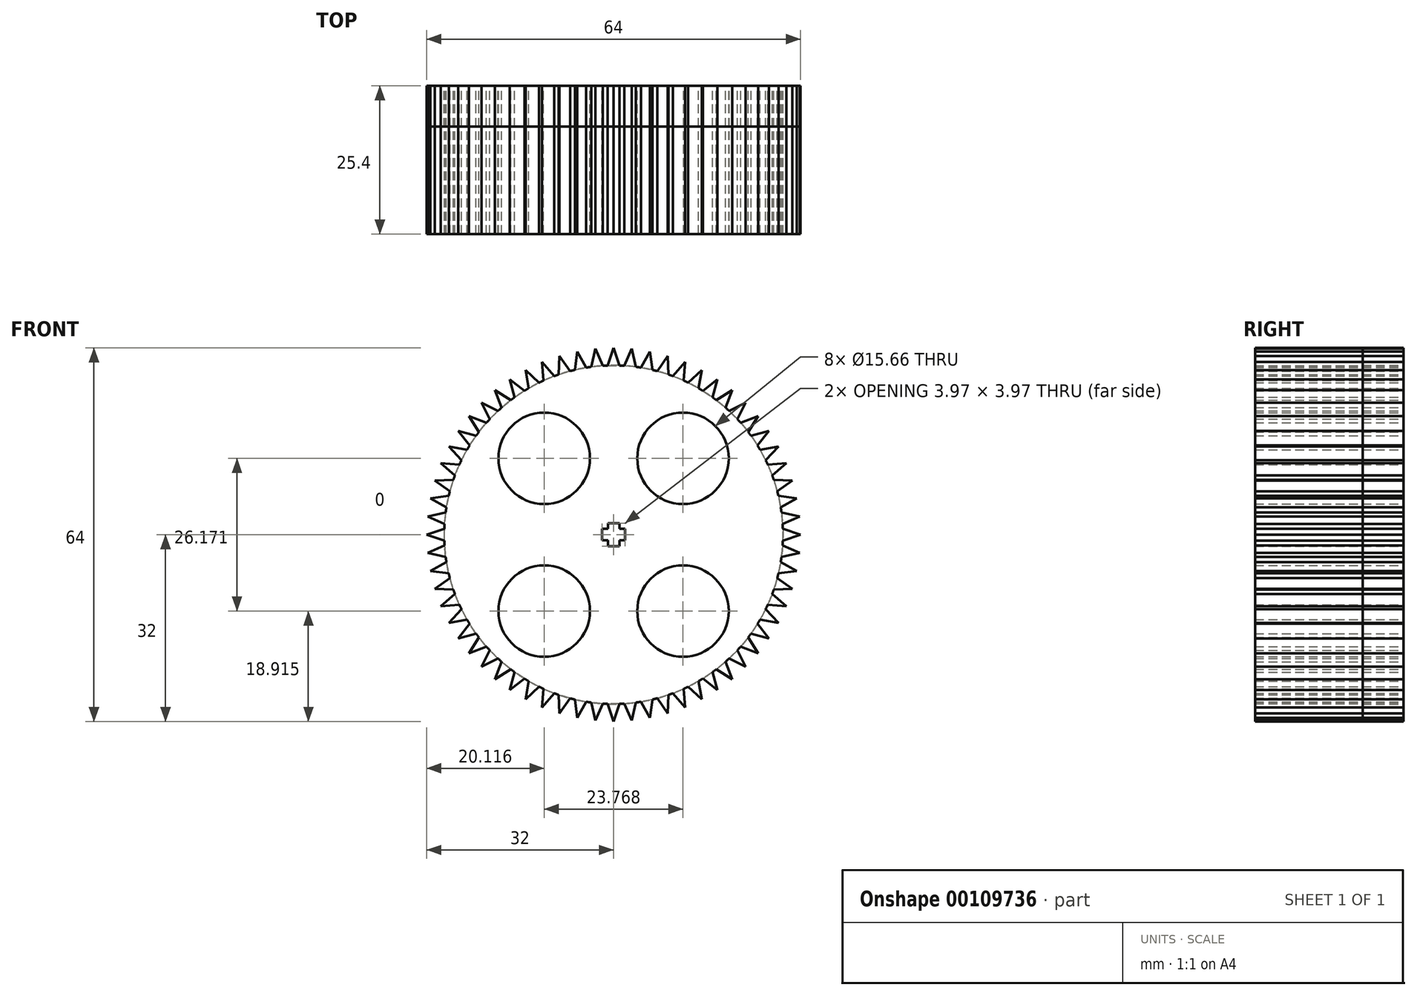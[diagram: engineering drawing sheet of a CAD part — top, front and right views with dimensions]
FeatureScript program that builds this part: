
annotation { "Feature Type Name" : "Feature", "Feature Type Description" : "" }
export const myFeature = defineFeature(function(context is Context, id is Id, definition is map)
    precondition{}
    {
        {
            var Q0;
            Q0=qCreatedBy(makeId("Front.planeOp"),FACE);
            var sketch = newSketch(context, id + "F0", { "sketchPlane" : qUnion([Q0])});
            skLineSegment(sketch, "E0", {"start": v(-0.98, 1.98) * mm, "end": v(-0.98, 0.98) * mm});
            skLineSegment(sketch, "E1", {"start": v(-0.98, 0.98) * mm, "end": v(-1.98, 0.98) * mm});
            skLineSegment(sketch, "E2.MirrorCS", {"start": v(0.98, 1.98) * mm, "end": v(0.98, 0.98) * mm});
            skLineSegment(sketch, "E3.MirrorCS", {"start": v(0.98, 0.98) * mm, "end": v(1.98, 0.98) * mm});
            skLineSegment(sketch, "E4.MirrorCS", {"start": v(0.98, -0.98) * mm, "end": v(1.98, -0.98) * mm});
            skLineSegment(sketch, "E5.MirrorCS", {"start": v(0.98, -1.98) * mm, "end": v(0.98, -0.98) * mm});
            skLineSegment(sketch, "E6.MirrorCS", {"start": v(-0.98, -1.98) * mm, "end": v(-0.98, -0.98) * mm});
            skLineSegment(sketch, "E7.MirrorCS", {"start": v(-0.98, -0.98) * mm, "end": v(-1.98, -0.98) * mm});
            skLineSegment(sketch, "E8", {"start": v(-0.98, 1.98) * mm, "end": v(0.98, 1.98) * mm});
            skLineSegment(sketch, "E9", {"start": v(-1.98, 0.98) * mm, "end": v(-1.98, -0.98) * mm});
            skLineSegment(sketch, "E10.MirrorCS", {"start": v(1.98, 0.98) * mm, "end": v(1.98, -0.98) * mm});
            skLineSegment(sketch, "E11.MirrorCS", {"start": v(-0.98, -1.98) * mm, "end": v(0.98, -1.98) * mm});
            skCircle(sketch, "E12", {"center": v(0, 0) * mm, "radius": 29 * mm});
            skLineSegment(sketch, "E13", {"start": v(-1, 28.98) * mm, "end": v(0, 32) * mm});
            skLineSegment(sketch, "E14.MirrorCS", {"start": v(1, 28.98) * mm, "end": v(0, 32) * mm});
            skLineSegment(sketch, "E15", {"start": v(-1, 28.98) * mm, "end": v(1, 28.98) * mm});
            skLineSegment(sketch, "E16.1.0", {"start": v(-1.85, 28.94) * mm, "end": v(-3.14, 31.85) * mm});
            skLineSegment(sketch, "E16.1.1", {"start": v(-3.84, 28.75) * mm, "end": v(-3.14, 31.85) * mm});
            skLineSegment(sketch, "E16.1.2", {"start": v(-3.84, 28.75) * mm, "end": v(-1.85, 28.94) * mm});
            skLineSegment(sketch, "E16.2.0", {"start": v(-4.67, 28.62) * mm, "end": v(-6.24, 31.39) * mm});
            skLineSegment(sketch, "E16.2.1", {"start": v(-6.64, 28.23) * mm, "end": v(-6.24, 31.39) * mm});
            skLineSegment(sketch, "E16.2.2", {"start": v(-6.64, 28.23) * mm, "end": v(-4.67, 28.62) * mm});
            skLineSegment(sketch, "E16.3.0", {"start": v(-7.46, 28.03) * mm, "end": v(-9.29, 30.62) * mm});
            skLineSegment(sketch, "E16.3.1", {"start": v(-9.37, 27.44) * mm, "end": v(-9.29, 30.62) * mm});
            skLineSegment(sketch, "E16.3.2", {"start": v(-9.37, 27.44) * mm, "end": v(-7.46, 28.03) * mm});
            skLineSegment(sketch, "E16.4.0", {"start": v(-10.17, 27.16) * mm, "end": v(-12.25, 29.56) * mm});
            skLineSegment(sketch, "E16.4.1", {"start": v(-12.02, 26.4) * mm, "end": v(-12.25, 29.56) * mm});
            skLineSegment(sketch, "E16.4.2", {"start": v(-12.02, 26.4) * mm, "end": v(-10.17, 27.16) * mm});
            skLineSegment(sketch, "E16.5.0", {"start": v(-12.78, 26.03) * mm, "end": v(-15.08, 28.22) * mm});
            skLineSegment(sketch, "E16.5.1", {"start": v(-14.54, 25.09) * mm, "end": v(-15.08, 28.22) * mm});
            skLineSegment(sketch, "E16.5.2", {"start": v(-14.54, 25.09) * mm, "end": v(-12.78, 26.03) * mm});
            skLineSegment(sketch, "E16.6.0", {"start": v(-15.27, 24.65) * mm, "end": v(-17.78, 26.6) * mm});
            skLineSegment(sketch, "E16.6.1", {"start": v(-16.93, 23.54) * mm, "end": v(-17.78, 26.6) * mm});
            skLineSegment(sketch, "E16.6.2", {"start": v(-16.93, 23.54) * mm, "end": v(-15.27, 24.65) * mm});
            skLineSegment(sketch, "E16.7.0", {"start": v(-17.61, 23.04) * mm, "end": v(-20.3, 24.74) * mm});
            skLineSegment(sketch, "E16.7.1", {"start": v(-19.16, 21.77) * mm, "end": v(-20.3, 24.74) * mm});
            skLineSegment(sketch, "E16.7.2", {"start": v(-19.16, 21.77) * mm, "end": v(-17.61, 23.04) * mm});
            skLineSegment(sketch, "E16.8.0", {"start": v(-19.79, 21.2) * mm, "end": v(-22.63, 22.63) * mm});
            skLineSegment(sketch, "E16.8.1", {"start": v(-21.2, 19.79) * mm, "end": v(-22.63, 22.63) * mm});
            skLineSegment(sketch, "E16.8.2", {"start": v(-21.2, 19.79) * mm, "end": v(-19.79, 21.2) * mm});
            skLineSegment(sketch, "E16.9.0", {"start": v(-21.77, 19.16) * mm, "end": v(-24.74, 20.3) * mm});
            skLineSegment(sketch, "E16.9.1", {"start": v(-23.04, 17.61) * mm, "end": v(-24.74, 20.3) * mm});
            skLineSegment(sketch, "E16.9.2", {"start": v(-23.04, 17.61) * mm, "end": v(-21.77, 19.16) * mm});
            skLineSegment(sketch, "E16.10.0", {"start": v(-23.54, 16.93) * mm, "end": v(-26.6, 17.78) * mm});
            skLineSegment(sketch, "E16.10.1", {"start": v(-24.65, 15.27) * mm, "end": v(-26.6, 17.78) * mm});
            skLineSegment(sketch, "E16.10.2", {"start": v(-24.65, 15.27) * mm, "end": v(-23.54, 16.93) * mm});
            skLineSegment(sketch, "E16.11.0", {"start": v(-25.09, 14.54) * mm, "end": v(-28.22, 15.08) * mm});
            skLineSegment(sketch, "E16.11.1", {"start": v(-26.03, 12.78) * mm, "end": v(-28.22, 15.08) * mm});
            skLineSegment(sketch, "E16.11.2", {"start": v(-26.03, 12.78) * mm, "end": v(-25.09, 14.54) * mm});
            skLineSegment(sketch, "E16.12.0", {"start": v(-26.4, 12.02) * mm, "end": v(-29.56, 12.25) * mm});
            skLineSegment(sketch, "E16.12.1", {"start": v(-27.16, 10.17) * mm, "end": v(-29.56, 12.25) * mm});
            skLineSegment(sketch, "E16.12.2", {"start": v(-27.16, 10.17) * mm, "end": v(-26.4, 12.02) * mm});
            skLineSegment(sketch, "E16.13.0", {"start": v(-27.44, 9.37) * mm, "end": v(-30.62, 9.29) * mm});
            skLineSegment(sketch, "E16.13.1", {"start": v(-28.03, 7.46) * mm, "end": v(-30.62, 9.29) * mm});
            skLineSegment(sketch, "E16.13.2", {"start": v(-28.03, 7.46) * mm, "end": v(-27.44, 9.37) * mm});
            skLineSegment(sketch, "E16.14.0", {"start": v(-28.23, 6.64) * mm, "end": v(-31.39, 6.24) * mm});
            skLineSegment(sketch, "E16.14.1", {"start": v(-28.62, 4.67) * mm, "end": v(-31.39, 6.24) * mm});
            skLineSegment(sketch, "E16.14.2", {"start": v(-28.62, 4.67) * mm, "end": v(-28.23, 6.64) * mm});
            skLineSegment(sketch, "E16.15.0", {"start": v(-28.75, 3.84) * mm, "end": v(-31.85, 3.14) * mm});
            skLineSegment(sketch, "E16.15.1", {"start": v(-28.94, 1.85) * mm, "end": v(-31.85, 3.14) * mm});
            skLineSegment(sketch, "E16.15.2", {"start": v(-28.94, 1.85) * mm, "end": v(-28.75, 3.84) * mm});
            skLineSegment(sketch, "E16.16.0", {"start": v(-28.98, 1) * mm, "end": v(-32, 0) * mm});
            skLineSegment(sketch, "E16.16.1", {"start": v(-28.98, -1) * mm, "end": v(-32, 0) * mm});
            skLineSegment(sketch, "E16.16.2", {"start": v(-28.98, -1) * mm, "end": v(-28.98, 1) * mm});
            skLineSegment(sketch, "E16.17.0", {"start": v(-28.94, -1.85) * mm, "end": v(-31.85, -3.14) * mm});
            skLineSegment(sketch, "E16.17.1", {"start": v(-28.75, -3.84) * mm, "end": v(-31.85, -3.14) * mm});
            skLineSegment(sketch, "E16.17.2", {"start": v(-28.75, -3.84) * mm, "end": v(-28.94, -1.85) * mm});
            skLineSegment(sketch, "E16.18.0", {"start": v(-28.62, -4.67) * mm, "end": v(-31.39, -6.24) * mm});
            skLineSegment(sketch, "E16.18.1", {"start": v(-28.23, -6.64) * mm, "end": v(-31.39, -6.24) * mm});
            skLineSegment(sketch, "E16.18.2", {"start": v(-28.23, -6.64) * mm, "end": v(-28.62, -4.67) * mm});
            skLineSegment(sketch, "E16.19.0", {"start": v(-28.03, -7.46) * mm, "end": v(-30.62, -9.29) * mm});
            skLineSegment(sketch, "E16.19.1", {"start": v(-27.44, -9.37) * mm, "end": v(-30.62, -9.29) * mm});
            skLineSegment(sketch, "E16.19.2", {"start": v(-27.44, -9.37) * mm, "end": v(-28.03, -7.46) * mm});
            skLineSegment(sketch, "E16.20.0", {"start": v(-27.16, -10.17) * mm, "end": v(-29.56, -12.25) * mm});
            skLineSegment(sketch, "E16.20.1", {"start": v(-26.4, -12.02) * mm, "end": v(-29.56, -12.25) * mm});
            skLineSegment(sketch, "E16.20.2", {"start": v(-26.4, -12.02) * mm, "end": v(-27.16, -10.17) * mm});
            skLineSegment(sketch, "E16.21.0", {"start": v(-26.03, -12.78) * mm, "end": v(-28.22, -15.08) * mm});
            skLineSegment(sketch, "E16.21.1", {"start": v(-25.09, -14.54) * mm, "end": v(-28.22, -15.08) * mm});
            skLineSegment(sketch, "E16.21.2", {"start": v(-25.09, -14.54) * mm, "end": v(-26.03, -12.78) * mm});
            skLineSegment(sketch, "E16.22.0", {"start": v(-24.65, -15.27) * mm, "end": v(-26.6, -17.78) * mm});
            skLineSegment(sketch, "E16.22.1", {"start": v(-23.54, -16.93) * mm, "end": v(-26.6, -17.78) * mm});
            skLineSegment(sketch, "E16.22.2", {"start": v(-23.54, -16.93) * mm, "end": v(-24.65, -15.27) * mm});
            skLineSegment(sketch, "E16.23.0", {"start": v(-23.04, -17.61) * mm, "end": v(-24.74, -20.3) * mm});
            skLineSegment(sketch, "E16.23.1", {"start": v(-21.77, -19.16) * mm, "end": v(-24.74, -20.3) * mm});
            skLineSegment(sketch, "E16.23.2", {"start": v(-21.77, -19.16) * mm, "end": v(-23.04, -17.61) * mm});
            skLineSegment(sketch, "E16.24.0", {"start": v(-21.2, -19.79) * mm, "end": v(-22.63, -22.63) * mm});
            skLineSegment(sketch, "E16.24.1", {"start": v(-19.79, -21.2) * mm, "end": v(-22.63, -22.63) * mm});
            skLineSegment(sketch, "E16.24.2", {"start": v(-19.79, -21.2) * mm, "end": v(-21.2, -19.79) * mm});
            skLineSegment(sketch, "E16.25.0", {"start": v(-19.16, -21.77) * mm, "end": v(-20.3, -24.74) * mm});
            skLineSegment(sketch, "E16.25.1", {"start": v(-17.61, -23.04) * mm, "end": v(-20.3, -24.74) * mm});
            skLineSegment(sketch, "E16.25.2", {"start": v(-17.61, -23.04) * mm, "end": v(-19.16, -21.77) * mm});
            skLineSegment(sketch, "E16.26.0", {"start": v(-16.93, -23.54) * mm, "end": v(-17.78, -26.6) * mm});
            skLineSegment(sketch, "E16.26.1", {"start": v(-15.27, -24.65) * mm, "end": v(-17.78, -26.6) * mm});
            skLineSegment(sketch, "E16.26.2", {"start": v(-15.27, -24.65) * mm, "end": v(-16.93, -23.54) * mm});
            skLineSegment(sketch, "E16.27.0", {"start": v(-14.54, -25.09) * mm, "end": v(-15.08, -28.22) * mm});
            skLineSegment(sketch, "E16.27.1", {"start": v(-12.78, -26.03) * mm, "end": v(-15.08, -28.22) * mm});
            skLineSegment(sketch, "E16.27.2", {"start": v(-12.78, -26.03) * mm, "end": v(-14.54, -25.09) * mm});
            skLineSegment(sketch, "E16.28.0", {"start": v(-12.02, -26.4) * mm, "end": v(-12.25, -29.56) * mm});
            skLineSegment(sketch, "E16.28.1", {"start": v(-10.17, -27.16) * mm, "end": v(-12.25, -29.56) * mm});
            skLineSegment(sketch, "E16.28.2", {"start": v(-10.17, -27.16) * mm, "end": v(-12.02, -26.4) * mm});
            skLineSegment(sketch, "E16.29.0", {"start": v(-9.37, -27.44) * mm, "end": v(-9.29, -30.62) * mm});
            skLineSegment(sketch, "E16.29.1", {"start": v(-7.46, -28.03) * mm, "end": v(-9.29, -30.62) * mm});
            skLineSegment(sketch, "E16.29.2", {"start": v(-7.46, -28.03) * mm, "end": v(-9.37, -27.44) * mm});
            skLineSegment(sketch, "E16.30.0", {"start": v(-6.64, -28.23) * mm, "end": v(-6.24, -31.39) * mm});
            skLineSegment(sketch, "E16.30.1", {"start": v(-4.67, -28.62) * mm, "end": v(-6.24, -31.39) * mm});
            skLineSegment(sketch, "E16.30.2", {"start": v(-4.67, -28.62) * mm, "end": v(-6.64, -28.23) * mm});
            skLineSegment(sketch, "E16.31.0", {"start": v(-3.84, -28.75) * mm, "end": v(-3.14, -31.85) * mm});
            skLineSegment(sketch, "E16.31.1", {"start": v(-1.85, -28.94) * mm, "end": v(-3.14, -31.85) * mm});
            skLineSegment(sketch, "E16.31.2", {"start": v(-1.85, -28.94) * mm, "end": v(-3.84, -28.75) * mm});
            skLineSegment(sketch, "E16.32.0", {"start": v(-1, -28.98) * mm, "end": v(0, -32) * mm});
            skLineSegment(sketch, "E16.32.1", {"start": v(1, -28.98) * mm, "end": v(0, -32) * mm});
            skLineSegment(sketch, "E16.32.2", {"start": v(1, -28.98) * mm, "end": v(-1, -28.98) * mm});
            skLineSegment(sketch, "E16.33.0", {"start": v(1.85, -28.94) * mm, "end": v(3.14, -31.85) * mm});
            skLineSegment(sketch, "E16.33.1", {"start": v(3.84, -28.75) * mm, "end": v(3.14, -31.85) * mm});
            skLineSegment(sketch, "E16.33.2", {"start": v(3.84, -28.75) * mm, "end": v(1.85, -28.94) * mm});
            skLineSegment(sketch, "E16.34.0", {"start": v(4.67, -28.62) * mm, "end": v(6.24, -31.39) * mm});
            skLineSegment(sketch, "E16.34.1", {"start": v(6.64, -28.23) * mm, "end": v(6.24, -31.39) * mm});
            skLineSegment(sketch, "E16.34.2", {"start": v(6.64, -28.23) * mm, "end": v(4.67, -28.62) * mm});
            skLineSegment(sketch, "E16.35.0", {"start": v(7.46, -28.03) * mm, "end": v(9.29, -30.62) * mm});
            skLineSegment(sketch, "E16.35.1", {"start": v(9.37, -27.44) * mm, "end": v(9.29, -30.62) * mm});
            skLineSegment(sketch, "E16.35.2", {"start": v(9.37, -27.44) * mm, "end": v(7.46, -28.03) * mm});
            skLineSegment(sketch, "E16.36.0", {"start": v(10.17, -27.16) * mm, "end": v(12.25, -29.56) * mm});
            skLineSegment(sketch, "E16.36.1", {"start": v(12.02, -26.4) * mm, "end": v(12.25, -29.56) * mm});
            skLineSegment(sketch, "E16.36.2", {"start": v(12.02, -26.4) * mm, "end": v(10.17, -27.16) * mm});
            skLineSegment(sketch, "E16.37.0", {"start": v(12.78, -26.03) * mm, "end": v(15.08, -28.22) * mm});
            skLineSegment(sketch, "E16.37.1", {"start": v(14.54, -25.09) * mm, "end": v(15.08, -28.22) * mm});
            skLineSegment(sketch, "E16.37.2", {"start": v(14.54, -25.09) * mm, "end": v(12.78, -26.03) * mm});
            skLineSegment(sketch, "E16.38.0", {"start": v(15.27, -24.65) * mm, "end": v(17.78, -26.6) * mm});
            skLineSegment(sketch, "E16.38.1", {"start": v(16.93, -23.54) * mm, "end": v(17.78, -26.6) * mm});
            skLineSegment(sketch, "E16.38.2", {"start": v(16.93, -23.54) * mm, "end": v(15.27, -24.65) * mm});
            skLineSegment(sketch, "E16.39.0", {"start": v(17.61, -23.04) * mm, "end": v(20.3, -24.74) * mm});
            skLineSegment(sketch, "E16.39.1", {"start": v(19.16, -21.77) * mm, "end": v(20.3, -24.74) * mm});
            skLineSegment(sketch, "E16.39.2", {"start": v(19.16, -21.77) * mm, "end": v(17.61, -23.04) * mm});
            skLineSegment(sketch, "E16.40.0", {"start": v(19.79, -21.2) * mm, "end": v(22.63, -22.63) * mm});
            skLineSegment(sketch, "E16.40.1", {"start": v(21.2, -19.79) * mm, "end": v(22.63, -22.63) * mm});
            skLineSegment(sketch, "E16.40.2", {"start": v(21.2, -19.79) * mm, "end": v(19.79, -21.2) * mm});
            skLineSegment(sketch, "E16.41.0", {"start": v(21.77, -19.16) * mm, "end": v(24.74, -20.3) * mm});
            skLineSegment(sketch, "E16.41.1", {"start": v(23.04, -17.61) * mm, "end": v(24.74, -20.3) * mm});
            skLineSegment(sketch, "E16.41.2", {"start": v(23.04, -17.61) * mm, "end": v(21.77, -19.16) * mm});
            skLineSegment(sketch, "E16.42.0", {"start": v(23.54, -16.93) * mm, "end": v(26.6, -17.78) * mm});
            skLineSegment(sketch, "E16.42.1", {"start": v(24.65, -15.27) * mm, "end": v(26.6, -17.78) * mm});
            skLineSegment(sketch, "E16.42.2", {"start": v(24.65, -15.27) * mm, "end": v(23.54, -16.93) * mm});
            skLineSegment(sketch, "E16.43.0", {"start": v(25.09, -14.54) * mm, "end": v(28.22, -15.08) * mm});
            skLineSegment(sketch, "E16.43.1", {"start": v(26.03, -12.78) * mm, "end": v(28.22, -15.08) * mm});
            skLineSegment(sketch, "E16.43.2", {"start": v(26.03, -12.78) * mm, "end": v(25.09, -14.54) * mm});
            skLineSegment(sketch, "E16.44.0", {"start": v(26.4, -12.02) * mm, "end": v(29.56, -12.25) * mm});
            skLineSegment(sketch, "E16.44.1", {"start": v(27.16, -10.17) * mm, "end": v(29.56, -12.25) * mm});
            skLineSegment(sketch, "E16.44.2", {"start": v(27.16, -10.17) * mm, "end": v(26.4, -12.02) * mm});
            skLineSegment(sketch, "E16.45.0", {"start": v(27.44, -9.37) * mm, "end": v(30.62, -9.29) * mm});
            skLineSegment(sketch, "E16.45.1", {"start": v(28.03, -7.46) * mm, "end": v(30.62, -9.29) * mm});
            skLineSegment(sketch, "E16.45.2", {"start": v(28.03, -7.46) * mm, "end": v(27.44, -9.37) * mm});
            skLineSegment(sketch, "E16.46.0", {"start": v(28.23, -6.64) * mm, "end": v(31.39, -6.24) * mm});
            skLineSegment(sketch, "E16.46.1", {"start": v(28.62, -4.67) * mm, "end": v(31.39, -6.24) * mm});
            skLineSegment(sketch, "E16.46.2", {"start": v(28.62, -4.67) * mm, "end": v(28.23, -6.64) * mm});
            skLineSegment(sketch, "E16.47.0", {"start": v(28.75, -3.84) * mm, "end": v(31.85, -3.14) * mm});
            skLineSegment(sketch, "E16.47.1", {"start": v(28.94, -1.85) * mm, "end": v(31.85, -3.14) * mm});
            skLineSegment(sketch, "E16.47.2", {"start": v(28.94, -1.85) * mm, "end": v(28.75, -3.84) * mm});
            skLineSegment(sketch, "E16.48.0", {"start": v(28.98, -1) * mm, "end": v(32, 0) * mm});
            skLineSegment(sketch, "E16.48.1", {"start": v(28.98, 1) * mm, "end": v(32, 0) * mm});
            skLineSegment(sketch, "E16.48.2", {"start": v(28.98, 1) * mm, "end": v(28.98, -1) * mm});
            skLineSegment(sketch, "E16.49.0", {"start": v(28.94, 1.85) * mm, "end": v(31.85, 3.14) * mm});
            skLineSegment(sketch, "E16.49.1", {"start": v(28.75, 3.84) * mm, "end": v(31.85, 3.14) * mm});
            skLineSegment(sketch, "E16.49.2", {"start": v(28.75, 3.84) * mm, "end": v(28.94, 1.85) * mm});
            skLineSegment(sketch, "E16.50.0", {"start": v(28.62, 4.67) * mm, "end": v(31.39, 6.24) * mm});
            skLineSegment(sketch, "E16.50.1", {"start": v(28.23, 6.64) * mm, "end": v(31.39, 6.24) * mm});
            skLineSegment(sketch, "E16.50.2", {"start": v(28.23, 6.64) * mm, "end": v(28.62, 4.67) * mm});
            skLineSegment(sketch, "E16.51.0", {"start": v(28.03, 7.46) * mm, "end": v(30.62, 9.29) * mm});
            skLineSegment(sketch, "E16.51.1", {"start": v(27.44, 9.37) * mm, "end": v(30.62, 9.29) * mm});
            skLineSegment(sketch, "E16.51.2", {"start": v(27.44, 9.37) * mm, "end": v(28.03, 7.46) * mm});
            skLineSegment(sketch, "E16.52.0", {"start": v(27.16, 10.17) * mm, "end": v(29.56, 12.25) * mm});
            skLineSegment(sketch, "E16.52.1", {"start": v(26.4, 12.02) * mm, "end": v(29.56, 12.25) * mm});
            skLineSegment(sketch, "E16.52.2", {"start": v(26.4, 12.02) * mm, "end": v(27.16, 10.17) * mm});
            skLineSegment(sketch, "E16.53.0", {"start": v(26.03, 12.78) * mm, "end": v(28.22, 15.08) * mm});
            skLineSegment(sketch, "E16.53.1", {"start": v(25.09, 14.54) * mm, "end": v(28.22, 15.08) * mm});
            skLineSegment(sketch, "E16.53.2", {"start": v(25.09, 14.54) * mm, "end": v(26.03, 12.78) * mm});
            skLineSegment(sketch, "E16.54.0", {"start": v(24.65, 15.27) * mm, "end": v(26.6, 17.78) * mm});
            skLineSegment(sketch, "E16.54.1", {"start": v(23.54, 16.93) * mm, "end": v(26.6, 17.78) * mm});
            skLineSegment(sketch, "E16.54.2", {"start": v(23.54, 16.93) * mm, "end": v(24.65, 15.27) * mm});
            skLineSegment(sketch, "E16.55.0", {"start": v(23.04, 17.61) * mm, "end": v(24.74, 20.3) * mm});
            skLineSegment(sketch, "E16.55.1", {"start": v(21.77, 19.16) * mm, "end": v(24.74, 20.3) * mm});
            skLineSegment(sketch, "E16.55.2", {"start": v(21.77, 19.16) * mm, "end": v(23.04, 17.61) * mm});
            skLineSegment(sketch, "E16.56.0", {"start": v(21.2, 19.79) * mm, "end": v(22.63, 22.63) * mm});
            skLineSegment(sketch, "E16.56.1", {"start": v(19.79, 21.2) * mm, "end": v(22.63, 22.63) * mm});
            skLineSegment(sketch, "E16.56.2", {"start": v(19.79, 21.2) * mm, "end": v(21.2, 19.79) * mm});
            skLineSegment(sketch, "E16.57.0", {"start": v(19.16, 21.77) * mm, "end": v(20.3, 24.74) * mm});
            skLineSegment(sketch, "E16.57.1", {"start": v(17.61, 23.04) * mm, "end": v(20.3, 24.74) * mm});
            skLineSegment(sketch, "E16.57.2", {"start": v(17.61, 23.04) * mm, "end": v(19.16, 21.77) * mm});
            skLineSegment(sketch, "E16.58.0", {"start": v(16.93, 23.54) * mm, "end": v(17.78, 26.6) * mm});
            skLineSegment(sketch, "E16.58.1", {"start": v(15.27, 24.65) * mm, "end": v(17.78, 26.6) * mm});
            skLineSegment(sketch, "E16.58.2", {"start": v(15.27, 24.65) * mm, "end": v(16.93, 23.54) * mm});
            skLineSegment(sketch, "E16.59.0", {"start": v(14.54, 25.09) * mm, "end": v(15.08, 28.22) * mm});
            skLineSegment(sketch, "E16.59.1", {"start": v(12.78, 26.03) * mm, "end": v(15.08, 28.22) * mm});
            skLineSegment(sketch, "E16.59.2", {"start": v(12.78, 26.03) * mm, "end": v(14.54, 25.09) * mm});
            skLineSegment(sketch, "E16.60.0", {"start": v(12.02, 26.4) * mm, "end": v(12.25, 29.56) * mm});
            skLineSegment(sketch, "E16.60.1", {"start": v(10.17, 27.16) * mm, "end": v(12.25, 29.56) * mm});
            skLineSegment(sketch, "E16.60.2", {"start": v(10.17, 27.16) * mm, "end": v(12.02, 26.4) * mm});
            skLineSegment(sketch, "E16.61.0", {"start": v(9.37, 27.44) * mm, "end": v(9.29, 30.62) * mm});
            skLineSegment(sketch, "E16.61.1", {"start": v(7.46, 28.03) * mm, "end": v(9.29, 30.62) * mm});
            skLineSegment(sketch, "E16.61.2", {"start": v(7.46, 28.03) * mm, "end": v(9.37, 27.44) * mm});
            skLineSegment(sketch, "E16.62.0", {"start": v(6.64, 28.23) * mm, "end": v(6.24, 31.39) * mm});
            skLineSegment(sketch, "E16.62.1", {"start": v(4.67, 28.62) * mm, "end": v(6.24, 31.39) * mm});
            skLineSegment(sketch, "E16.62.2", {"start": v(4.67, 28.62) * mm, "end": v(6.64, 28.23) * mm});
            skLineSegment(sketch, "E16.63.0", {"start": v(3.84, 28.75) * mm, "end": v(3.14, 31.85) * mm});
            skLineSegment(sketch, "E16.63.1", {"start": v(1.85, 28.94) * mm, "end": v(3.14, 31.85) * mm});
            skLineSegment(sketch, "E16.63.2", {"start": v(1.85, 28.94) * mm, "end": v(3.84, 28.75) * mm});
            skCircle(sketch, "E17", {"center": v(-11.88, 13.09) * mm, "radius": 7.83 * mm});
            skCircle(sketch, "E18.MirrorC", {"center": v(11.88, 13.09) * mm, "radius": 7.83 * mm});
            skCircle(sketch, "E19.MirrorC", {"center": v(11.88, -13.09) * mm, "radius": 7.83 * mm});
            skCircle(sketch, "E20.MirrorC", {"center": v(-11.88, -13.09) * mm, "radius": 7.83 * mm});
            skLineSegment(sketch, "E21", {"start": v(0, 32) * mm, "end": v(0, -32) * mm, "construction": true});
            skSolve(sketch);
        }
        {
            var Q0;
            {var subQ1=sQuery(id+"F0.wireOp",EDGE,"E13");Q0=makeQuery(id+"F0.imprint","IMPRINT",FACE,{"disambiguationData":[TD([[makeQuery(id+"F0.imprint","IMPRINT",EDGE,{"derivedFrom":subQ1}),-1.0]])]});}
            var Q1;
            {var subQ1=sQuery(id+"F0.wireOp",EDGE,"E16.63.0");Q1=makeQuery(id+"F0.imprint","IMPRINT",FACE,{"disambiguationData":[TD([[makeQuery(id+"F0.imprint","IMPRINT",EDGE,{"derivedFrom":subQ1}),1.0]])]});}
            var Q2;
            {var subQ1=sQuery(id+"F0.wireOp",EDGE,"E16.62.0");Q2=makeQuery(id+"F0.imprint","IMPRINT",FACE,{"disambiguationData":[TD([[makeQuery(id+"F0.imprint","IMPRINT",EDGE,{"derivedFrom":subQ1}),1.0]])]});}
            var Q3;
            {var subQ1=sQuery(id+"F0.wireOp",EDGE,"E16.61.0");Q3=makeQuery(id+"F0.imprint","IMPRINT",FACE,{"disambiguationData":[TD([[makeQuery(id+"F0.imprint","IMPRINT",EDGE,{"derivedFrom":subQ1}),1.0]])]});}
            var Q4;
            {var subQ1=sQuery(id+"F0.wireOp",EDGE,"E16.60.0");Q4=makeQuery(id+"F0.imprint","IMPRINT",FACE,{"disambiguationData":[TD([[makeQuery(id+"F0.imprint","IMPRINT",EDGE,{"derivedFrom":subQ1}),1.0]])]});}
            var Q5;
            {var subQ1=sQuery(id+"F0.wireOp",EDGE,"E16.59.0");Q5=makeQuery(id+"F0.imprint","IMPRINT",FACE,{"disambiguationData":[TD([[makeQuery(id+"F0.imprint","IMPRINT",EDGE,{"derivedFrom":subQ1}),1.0]])]});}
            var Q6;
            Q6=makeQuery(id+"F0.imprint","IMPRINT",FACE,{"disambiguationData":[TD([[makeQuery(id+"F0.imprint","IMPRINT",EDGE,{"derivedFrom":sQuery(id+"F0.wireOp",EDGE,"E0")}),-1.0]])]});
            var Q7;
            {var subQ1=sQuery(id+"F0.wireOp",EDGE,"E16.58.0");Q7=makeQuery(id+"F0.imprint","IMPRINT",FACE,{"disambiguationData":[TD([[makeQuery(id+"F0.imprint","IMPRINT",EDGE,{"derivedFrom":subQ1}),1.0]])]});}
            var Q8;
            {var subQ1=sQuery(id+"F0.wireOp",EDGE,"E16.57.0");Q8=makeQuery(id+"F0.imprint","IMPRINT",FACE,{"disambiguationData":[TD([[makeQuery(id+"F0.imprint","IMPRINT",EDGE,{"derivedFrom":subQ1}),1.0]])]});}
            var Q9;
            {var subQ1=sQuery(id+"F0.wireOp",EDGE,"E16.56.0");Q9=makeQuery(id+"F0.imprint","IMPRINT",FACE,{"disambiguationData":[TD([[makeQuery(id+"F0.imprint","IMPRINT",EDGE,{"derivedFrom":subQ1}),1.0]])]});}
            var Q10;
            {var subQ1=sQuery(id+"F0.wireOp",EDGE,"E16.55.0");Q10=makeQuery(id+"F0.imprint","IMPRINT",FACE,{"disambiguationData":[TD([[makeQuery(id+"F0.imprint","IMPRINT",EDGE,{"derivedFrom":subQ1}),1.0]])]});}
            var Q11;
            {var subQ1=sQuery(id+"F0.wireOp",EDGE,"E16.54.0");Q11=makeQuery(id+"F0.imprint","IMPRINT",FACE,{"disambiguationData":[TD([[makeQuery(id+"F0.imprint","IMPRINT",EDGE,{"derivedFrom":subQ1}),1.0]])]});}
            var Q12;
            {var subQ1=sQuery(id+"F0.wireOp",EDGE,"E16.53.0");Q12=makeQuery(id+"F0.imprint","IMPRINT",FACE,{"disambiguationData":[TD([[makeQuery(id+"F0.imprint","IMPRINT",EDGE,{"derivedFrom":subQ1}),1.0]])]});}
            var Q13;
            {var subQ1=sQuery(id+"F0.wireOp",EDGE,"E16.52.0");Q13=makeQuery(id+"F0.imprint","IMPRINT",FACE,{"disambiguationData":[TD([[makeQuery(id+"F0.imprint","IMPRINT",EDGE,{"derivedFrom":subQ1}),1.0]])]});}
            var Q14;
            {var subQ1=sQuery(id+"F0.wireOp",EDGE,"E16.51.0");Q14=makeQuery(id+"F0.imprint","IMPRINT",FACE,{"disambiguationData":[TD([[makeQuery(id+"F0.imprint","IMPRINT",EDGE,{"derivedFrom":subQ1}),1.0]])]});}
            var Q15;
            {var subQ1=sQuery(id+"F0.wireOp",EDGE,"E16.50.0");Q15=makeQuery(id+"F0.imprint","IMPRINT",FACE,{"disambiguationData":[TD([[makeQuery(id+"F0.imprint","IMPRINT",EDGE,{"derivedFrom":subQ1}),1.0]])]});}
            var Q16;
            {var subQ1=sQuery(id+"F0.wireOp",EDGE,"E16.49.0");Q16=makeQuery(id+"F0.imprint","IMPRINT",FACE,{"disambiguationData":[TD([[makeQuery(id+"F0.imprint","IMPRINT",EDGE,{"derivedFrom":subQ1}),1.0]])]});}
            var Q17;
            {var subQ1=sQuery(id+"F0.wireOp",EDGE,"E16.48.0");Q17=makeQuery(id+"F0.imprint","IMPRINT",FACE,{"disambiguationData":[TD([[makeQuery(id+"F0.imprint","IMPRINT",EDGE,{"derivedFrom":subQ1}),1.0]])]});}
            var Q18;
            {var subQ1=sQuery(id+"F0.wireOp",EDGE,"E16.47.0");Q18=makeQuery(id+"F0.imprint","IMPRINT",FACE,{"disambiguationData":[TD([[makeQuery(id+"F0.imprint","IMPRINT",EDGE,{"derivedFrom":subQ1}),1.0]])]});}
            var Q19;
            {var subQ1=sQuery(id+"F0.wireOp",EDGE,"E16.46.0");Q19=makeQuery(id+"F0.imprint","IMPRINT",FACE,{"disambiguationData":[TD([[makeQuery(id+"F0.imprint","IMPRINT",EDGE,{"derivedFrom":subQ1}),1.0]])]});}
            var Q20;
            {var subQ1=sQuery(id+"F0.wireOp",EDGE,"E16.45.0");Q20=makeQuery(id+"F0.imprint","IMPRINT",FACE,{"disambiguationData":[TD([[makeQuery(id+"F0.imprint","IMPRINT",EDGE,{"derivedFrom":subQ1}),1.0]])]});}
            var Q21;
            {var subQ1=sQuery(id+"F0.wireOp",EDGE,"E16.44.0");Q21=makeQuery(id+"F0.imprint","IMPRINT",FACE,{"disambiguationData":[TD([[makeQuery(id+"F0.imprint","IMPRINT",EDGE,{"derivedFrom":subQ1}),1.0]])]});}
            var Q22;
            {var subQ1=sQuery(id+"F0.wireOp",EDGE,"E16.42.0");Q22=makeQuery(id+"F0.imprint","IMPRINT",FACE,{"disambiguationData":[TD([[makeQuery(id+"F0.imprint","IMPRINT",EDGE,{"derivedFrom":subQ1}),1.0]])]});}
            var Q23;
            {var subQ1=sQuery(id+"F0.wireOp",EDGE,"E16.43.0");Q23=makeQuery(id+"F0.imprint","IMPRINT",FACE,{"disambiguationData":[TD([[makeQuery(id+"F0.imprint","IMPRINT",EDGE,{"derivedFrom":subQ1}),1.0]])]});}
            var Q24;
            {var subQ1=sQuery(id+"F0.wireOp",EDGE,"E16.41.0");Q24=makeQuery(id+"F0.imprint","IMPRINT",FACE,{"disambiguationData":[TD([[makeQuery(id+"F0.imprint","IMPRINT",EDGE,{"derivedFrom":subQ1}),1.0]])]});}
            var Q25;
            {var subQ1=sQuery(id+"F0.wireOp",EDGE,"E16.40.0");Q25=makeQuery(id+"F0.imprint","IMPRINT",FACE,{"disambiguationData":[TD([[makeQuery(id+"F0.imprint","IMPRINT",EDGE,{"derivedFrom":subQ1}),1.0]])]});}
            var Q26;
            {var subQ1=sQuery(id+"F0.wireOp",EDGE,"E16.39.0");Q26=makeQuery(id+"F0.imprint","IMPRINT",FACE,{"disambiguationData":[TD([[makeQuery(id+"F0.imprint","IMPRINT",EDGE,{"derivedFrom":subQ1}),1.0]])]});}
            var Q27;
            {var subQ1=sQuery(id+"F0.wireOp",EDGE,"E16.38.0");Q27=makeQuery(id+"F0.imprint","IMPRINT",FACE,{"disambiguationData":[TD([[makeQuery(id+"F0.imprint","IMPRINT",EDGE,{"derivedFrom":subQ1}),1.0]])]});}
            var Q28;
            {var subQ1=sQuery(id+"F0.wireOp",EDGE,"E16.37.0");Q28=makeQuery(id+"F0.imprint","IMPRINT",FACE,{"disambiguationData":[TD([[makeQuery(id+"F0.imprint","IMPRINT",EDGE,{"derivedFrom":subQ1}),1.0]])]});}
            var Q29;
            {var subQ1=sQuery(id+"F0.wireOp",EDGE,"E16.36.0");Q29=makeQuery(id+"F0.imprint","IMPRINT",FACE,{"disambiguationData":[TD([[makeQuery(id+"F0.imprint","IMPRINT",EDGE,{"derivedFrom":subQ1}),1.0]])]});}
            var Q30;
            {var subQ1=sQuery(id+"F0.wireOp",EDGE,"E16.35.0");Q30=makeQuery(id+"F0.imprint","IMPRINT",FACE,{"disambiguationData":[TD([[makeQuery(id+"F0.imprint","IMPRINT",EDGE,{"derivedFrom":subQ1}),1.0]])]});}
            var Q31;
            {var subQ1=sQuery(id+"F0.wireOp",EDGE,"E16.34.0");Q31=makeQuery(id+"F0.imprint","IMPRINT",FACE,{"disambiguationData":[TD([[makeQuery(id+"F0.imprint","IMPRINT",EDGE,{"derivedFrom":subQ1}),1.0]])]});}
            var Q32;
            {var subQ1=sQuery(id+"F0.wireOp",EDGE,"E16.33.0");Q32=makeQuery(id+"F0.imprint","IMPRINT",FACE,{"disambiguationData":[TD([[makeQuery(id+"F0.imprint","IMPRINT",EDGE,{"derivedFrom":subQ1}),1.0]])]});}
            var Q33;
            {var subQ1=sQuery(id+"F0.wireOp",EDGE,"E16.32.0");Q33=makeQuery(id+"F0.imprint","IMPRINT",FACE,{"disambiguationData":[TD([[makeQuery(id+"F0.imprint","IMPRINT",EDGE,{"derivedFrom":subQ1}),1.0]])]});}
            var Q34;
            {var subQ1=sQuery(id+"F0.wireOp",EDGE,"E16.31.0");Q34=makeQuery(id+"F0.imprint","IMPRINT",FACE,{"disambiguationData":[TD([[makeQuery(id+"F0.imprint","IMPRINT",EDGE,{"derivedFrom":subQ1}),1.0]])]});}
            var Q35;
            {var subQ1=sQuery(id+"F0.wireOp",EDGE,"E16.30.0");Q35=makeQuery(id+"F0.imprint","IMPRINT",FACE,{"disambiguationData":[TD([[makeQuery(id+"F0.imprint","IMPRINT",EDGE,{"derivedFrom":subQ1}),1.0]])]});}
            var Q36;
            {var subQ1=sQuery(id+"F0.wireOp",EDGE,"E16.29.0");Q36=makeQuery(id+"F0.imprint","IMPRINT",FACE,{"disambiguationData":[TD([[makeQuery(id+"F0.imprint","IMPRINT",EDGE,{"derivedFrom":subQ1}),1.0]])]});}
            var Q37;
            {var subQ1=sQuery(id+"F0.wireOp",EDGE,"E16.28.0");Q37=makeQuery(id+"F0.imprint","IMPRINT",FACE,{"disambiguationData":[TD([[makeQuery(id+"F0.imprint","IMPRINT",EDGE,{"derivedFrom":subQ1}),1.0]])]});}
            var Q38;
            {var subQ1=sQuery(id+"F0.wireOp",EDGE,"E16.27.0");Q38=makeQuery(id+"F0.imprint","IMPRINT",FACE,{"disambiguationData":[TD([[makeQuery(id+"F0.imprint","IMPRINT",EDGE,{"derivedFrom":subQ1}),1.0]])]});}
            var Q39;
            {var subQ1=sQuery(id+"F0.wireOp",EDGE,"E16.26.0");Q39=makeQuery(id+"F0.imprint","IMPRINT",FACE,{"disambiguationData":[TD([[makeQuery(id+"F0.imprint","IMPRINT",EDGE,{"derivedFrom":subQ1}),1.0]])]});}
            var Q40;
            {var subQ1=sQuery(id+"F0.wireOp",EDGE,"E16.25.0");Q40=makeQuery(id+"F0.imprint","IMPRINT",FACE,{"disambiguationData":[TD([[makeQuery(id+"F0.imprint","IMPRINT",EDGE,{"derivedFrom":subQ1}),1.0]])]});}
            var Q41;
            {var subQ1=sQuery(id+"F0.wireOp",EDGE,"E16.24.0");Q41=makeQuery(id+"F0.imprint","IMPRINT",FACE,{"disambiguationData":[TD([[makeQuery(id+"F0.imprint","IMPRINT",EDGE,{"derivedFrom":subQ1}),1.0]])]});}
            var Q42;
            {var subQ1=sQuery(id+"F0.wireOp",EDGE,"E16.23.0");Q42=makeQuery(id+"F0.imprint","IMPRINT",FACE,{"disambiguationData":[TD([[makeQuery(id+"F0.imprint","IMPRINT",EDGE,{"derivedFrom":subQ1}),1.0]])]});}
            var Q43;
            {var subQ1=sQuery(id+"F0.wireOp",EDGE,"E16.22.0");Q43=makeQuery(id+"F0.imprint","IMPRINT",FACE,{"disambiguationData":[TD([[makeQuery(id+"F0.imprint","IMPRINT",EDGE,{"derivedFrom":subQ1}),1.0]])]});}
            var Q44;
            {var subQ1=sQuery(id+"F0.wireOp",EDGE,"E16.21.0");Q44=makeQuery(id+"F0.imprint","IMPRINT",FACE,{"disambiguationData":[TD([[makeQuery(id+"F0.imprint","IMPRINT",EDGE,{"derivedFrom":subQ1}),1.0]])]});}
            var Q45;
            {var subQ1=sQuery(id+"F0.wireOp",EDGE,"E16.20.0");Q45=makeQuery(id+"F0.imprint","IMPRINT",FACE,{"disambiguationData":[TD([[makeQuery(id+"F0.imprint","IMPRINT",EDGE,{"derivedFrom":subQ1}),1.0]])]});}
            var Q46;
            {var subQ1=sQuery(id+"F0.wireOp",EDGE,"E16.19.0");Q46=makeQuery(id+"F0.imprint","IMPRINT",FACE,{"disambiguationData":[TD([[makeQuery(id+"F0.imprint","IMPRINT",EDGE,{"derivedFrom":subQ1}),1.0]])]});}
            var Q47;
            {var subQ1=sQuery(id+"F0.wireOp",EDGE,"E16.18.0");Q47=makeQuery(id+"F0.imprint","IMPRINT",FACE,{"disambiguationData":[TD([[makeQuery(id+"F0.imprint","IMPRINT",EDGE,{"derivedFrom":subQ1}),1.0]])]});}
            var Q48;
            {var subQ1=sQuery(id+"F0.wireOp",EDGE,"E16.17.0");Q48=makeQuery(id+"F0.imprint","IMPRINT",FACE,{"disambiguationData":[TD([[makeQuery(id+"F0.imprint","IMPRINT",EDGE,{"derivedFrom":subQ1}),1.0]])]});}
            var Q49;
            {var subQ1=sQuery(id+"F0.wireOp",EDGE,"E16.15.0");Q49=makeQuery(id+"F0.imprint","IMPRINT",FACE,{"disambiguationData":[TD([[makeQuery(id+"F0.imprint","IMPRINT",EDGE,{"derivedFrom":subQ1}),1.0]])]});}
            var Q50;
            {var subQ1=sQuery(id+"F0.wireOp",EDGE,"E16.16.0");Q50=makeQuery(id+"F0.imprint","IMPRINT",FACE,{"disambiguationData":[TD([[makeQuery(id+"F0.imprint","IMPRINT",EDGE,{"derivedFrom":subQ1}),1.0]])]});}
            var Q51;
            {var subQ1=sQuery(id+"F0.wireOp",EDGE,"E16.14.0");Q51=makeQuery(id+"F0.imprint","IMPRINT",FACE,{"disambiguationData":[TD([[makeQuery(id+"F0.imprint","IMPRINT",EDGE,{"derivedFrom":subQ1}),1.0]])]});}
            var Q52;
            {var subQ1=sQuery(id+"F0.wireOp",EDGE,"E16.13.0");Q52=makeQuery(id+"F0.imprint","IMPRINT",FACE,{"disambiguationData":[TD([[makeQuery(id+"F0.imprint","IMPRINT",EDGE,{"derivedFrom":subQ1}),1.0]])]});}
            var Q53;
            {var subQ1=sQuery(id+"F0.wireOp",EDGE,"E16.12.0");Q53=makeQuery(id+"F0.imprint","IMPRINT",FACE,{"disambiguationData":[TD([[makeQuery(id+"F0.imprint","IMPRINT",EDGE,{"derivedFrom":subQ1}),1.0]])]});}
            var Q54;
            {var subQ1=sQuery(id+"F0.wireOp",EDGE,"E16.11.0");Q54=makeQuery(id+"F0.imprint","IMPRINT",FACE,{"disambiguationData":[TD([[makeQuery(id+"F0.imprint","IMPRINT",EDGE,{"derivedFrom":subQ1}),1.0]])]});}
            var Q55;
            {var subQ1=sQuery(id+"F0.wireOp",EDGE,"E16.10.0");Q55=makeQuery(id+"F0.imprint","IMPRINT",FACE,{"disambiguationData":[TD([[makeQuery(id+"F0.imprint","IMPRINT",EDGE,{"derivedFrom":subQ1}),1.0]])]});}
            var Q56;
            {var subQ1=sQuery(id+"F0.wireOp",EDGE,"E16.9.0");Q56=makeQuery(id+"F0.imprint","IMPRINT",FACE,{"disambiguationData":[TD([[makeQuery(id+"F0.imprint","IMPRINT",EDGE,{"derivedFrom":subQ1}),1.0]])]});}
            var Q57;
            {var subQ1=sQuery(id+"F0.wireOp",EDGE,"E16.8.0");Q57=makeQuery(id+"F0.imprint","IMPRINT",FACE,{"disambiguationData":[TD([[makeQuery(id+"F0.imprint","IMPRINT",EDGE,{"derivedFrom":subQ1}),1.0]])]});}
            var Q58;
            {var subQ1=sQuery(id+"F0.wireOp",EDGE,"E16.7.0");Q58=makeQuery(id+"F0.imprint","IMPRINT",FACE,{"disambiguationData":[TD([[makeQuery(id+"F0.imprint","IMPRINT",EDGE,{"derivedFrom":subQ1}),1.0]])]});}
            var Q59;
            {var subQ1=sQuery(id+"F0.wireOp",EDGE,"E16.6.0");Q59=makeQuery(id+"F0.imprint","IMPRINT",FACE,{"disambiguationData":[TD([[makeQuery(id+"F0.imprint","IMPRINT",EDGE,{"derivedFrom":subQ1}),1.0]])]});}
            var Q60;
            {var subQ1=sQuery(id+"F0.wireOp",EDGE,"E16.5.0");Q60=makeQuery(id+"F0.imprint","IMPRINT",FACE,{"disambiguationData":[TD([[makeQuery(id+"F0.imprint","IMPRINT",EDGE,{"derivedFrom":subQ1}),1.0]])]});}
            var Q61;
            {var subQ1=sQuery(id+"F0.wireOp",EDGE,"E16.4.0");Q61=makeQuery(id+"F0.imprint","IMPRINT",FACE,{"disambiguationData":[TD([[makeQuery(id+"F0.imprint","IMPRINT",EDGE,{"derivedFrom":subQ1}),1.0]])]});}
            var Q62;
            {var subQ1=sQuery(id+"F0.wireOp",EDGE,"E16.3.0");Q62=makeQuery(id+"F0.imprint","IMPRINT",FACE,{"disambiguationData":[TD([[makeQuery(id+"F0.imprint","IMPRINT",EDGE,{"derivedFrom":subQ1}),1.0]])]});}
            var Q63;
            {var subQ1=sQuery(id+"F0.wireOp",EDGE,"E16.2.0");Q63=makeQuery(id+"F0.imprint","IMPRINT",FACE,{"disambiguationData":[TD([[makeQuery(id+"F0.imprint","IMPRINT",EDGE,{"derivedFrom":subQ1}),1.0]])]});}
            var Q64;
            {var subQ1=sQuery(id+"F0.wireOp",EDGE,"E16.1.0");Q64=makeQuery(id+"F0.imprint","IMPRINT",FACE,{"disambiguationData":[TD([[makeQuery(id+"F0.imprint","IMPRINT",EDGE,{"derivedFrom":subQ1}),1.0]])]});}
            extrude(context, id + "F1", {"entities" : qUnion([Q0, Q1, Q2, Q3, Q4, Q5, Q6, Q7, Q8, Q9, Q10, Q11, Q12, Q13, Q14, Q15, Q16, Q17, Q18, Q19, Q20, Q21, Q22, Q23, Q24, Q25, Q26, Q27, Q28, Q29, Q30, Q31, Q32, Q33, Q34, Q35, Q36, Q37, Q38, Q39, Q40, Q41, Q42, Q43, Q44, Q45, Q46, Q47, Q48, Q49, Q50, Q51, Q52, Q53, Q54, Q55, Q56, Q57, Q58, Q59, Q60, Q61, Q62, Q63, Q64]), "depth" : 7 * mm});
        }
        {
            var Q0;
            Q0 = qSketchRegion(id + "F0", true);
            extrude(context, id + "F2", {"entities" : qUnion([Q0]), "depth" : 25.4 * mm});
        }
    });
